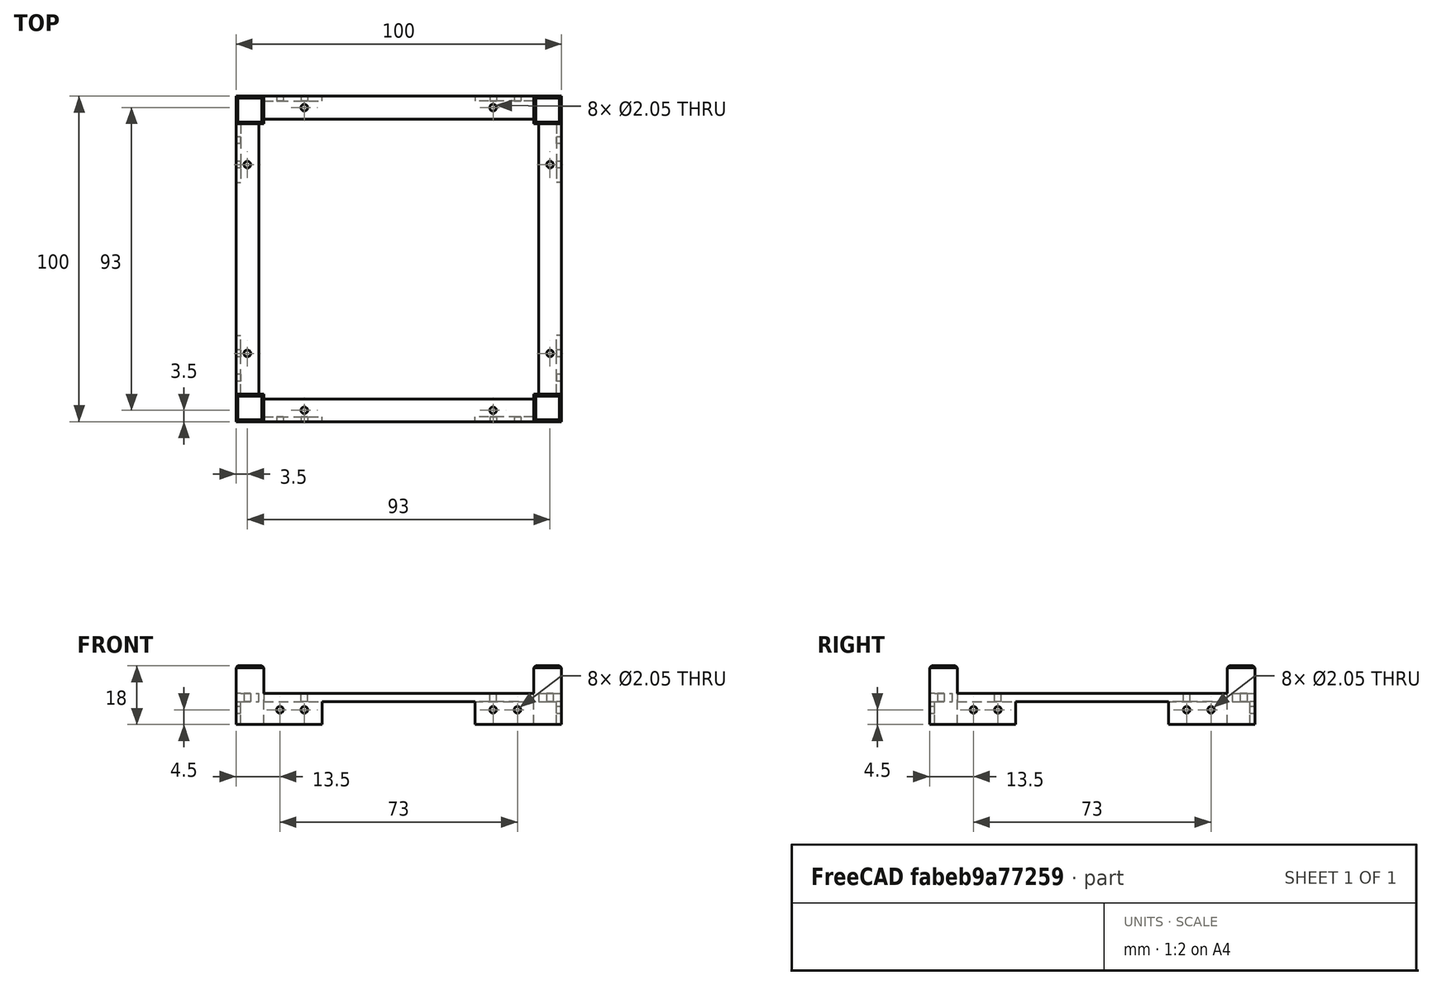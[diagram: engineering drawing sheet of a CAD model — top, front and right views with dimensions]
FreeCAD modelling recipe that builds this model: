
FCSTD DOCUMENT  (FreeCAD 0.20R29603 (Git))
Label: OpenSCAD_MyChassisModeling
License: All rights reserved
LicenseURL: http://en.wikipedia.org/wiki/All_rights_reserved
objects: Part::Box×72, Part::Fuse×56, Part::Cylinder×32, Part::Cut×17, Part::MultiFuse×13, Part::Mirroring×8, TechDraw::DrawViewDimension×5, TechDraw::DrawViewPart×3, TechDraw::DrawSVGTemplate×1, TechDraw::DrawViewAnnotation×1, TechDraw::DrawPage×1
note: 198 computed .brp shape members not serialized (recipe doc carries the construction recipe); baked Part::Feature solids carry a one-line shape summary decoded from their .brp

FEATURE [Part::Box] cube
  AttacherType = Attacher::AttachEngine3D
  Height = 2.5
  Length = 100
  Placement = pos=(-50,-3.5,-2.5) rot=(0,0,1;0rad)
  Width = 7
FEATURE [Part::Cylinder] cylinder
  Angle = 360
  AttacherType = Attacher::AttachEngine3D
  FirstAngle = 0
  Height = 100
  Placement = pos=(-29,0,-50) rot=(0,0,1;0rad)
  Radius = 1.025
  SecondAngle = 0
FEATURE [Part::Cylinder] cylinder001
  Angle = 360
  AttacherType = Attacher::AttachEngine3D
  FirstAngle = 0
  Height = 100
  Placement = pos=(29,0,-50) rot=(0,0,1;0rad)
  Radius = 1.025
  SecondAngle = 0
FEATURE [Part::Fuse] Group
  Base = -> cylinder
  Tool = -> cylinder001
FEATURE [Part::Cut] difference
  Base = -> cube
  Placement = pos=(0,46.5,0) rot=(0,0,1;0rad)
  Tool = -> Group
FEATURE [Part::Box] cube001
  AttacherType = Attacher::AttachEngine3D
  Height = 2.5
  Length = 100
  Placement = pos=(-50,-3.5,-2.5) rot=(0,0,1;0rad)
  Width = 7
FEATURE [Part::Cylinder] cylinder002
  Angle = 360
  AttacherType = Attacher::AttachEngine3D
  FirstAngle = 0
  Height = 100
  Placement = pos=(-29,0,-50) rot=(0,0,1;0rad)
  Radius = 1.025
  SecondAngle = 0
FEATURE [Part::Cylinder] cylinder003
  Angle = 360
  AttacherType = Attacher::AttachEngine3D
  FirstAngle = 0
  Height = 100
  Placement = pos=(29,0,-50) rot=(0,0,1;0rad)
  Radius = 1.025
  SecondAngle = 0
FEATURE [Part::Fuse] Group001
  Base = -> cylinder002
  Tool = -> cylinder003
FEATURE [Part::Cut] difference001
  Base = -> cube001
  Placement = pos=(0,46.5,0) rot=(0,0,1;0rad)
  Tool = -> Group001
FEATURE [Part::Fuse] Group002
  Base = -> difference
  Tool = -> difference001
FEATURE [Part::Box] cube002
  AttacherType = Attacher::AttachEngine3D
  Height = 2.5
  Length = 100
  Placement = pos=(-50,-3.5,-2.5) rot=(0,0,1;0rad)
  Width = 7
FEATURE [Part::Cylinder] cylinder004
  Angle = 360
  AttacherType = Attacher::AttachEngine3D
  FirstAngle = 0
  Height = 100
  Placement = pos=(-29,0,-50) rot=(0,0,1;0rad)
  Radius = 1.025
  SecondAngle = 0
FEATURE [Part::Cylinder] cylinder005
  Angle = 360
  AttacherType = Attacher::AttachEngine3D
  FirstAngle = 0
  Height = 100
  Placement = pos=(29,0,-50) rot=(0,0,1;0rad)
  Radius = 1.025
  SecondAngle = 0
FEATURE [Part::Fuse] Group003
  Base = -> cylinder004
  Tool = -> cylinder005
FEATURE [Part::Cut] difference002
  Base = -> cube002
  Placement = pos=(0,46.5,0) rot=(0,0,1;0rad)
  Tool = -> Group003
FEATURE [Part::Box] cube003
  AttacherType = Attacher::AttachEngine3D
  Height = 2.5
  Length = 100
  Placement = pos=(-50,-3.5,-2.5) rot=(0,0,1;0rad)
  Width = 7
FEATURE [Part::Cylinder] cylinder006
  Angle = 360
  AttacherType = Attacher::AttachEngine3D
  FirstAngle = 0
  Height = 100
  Placement = pos=(-29,0,-50) rot=(0,0,1;0rad)
  Radius = 1.025
  SecondAngle = 0
FEATURE [Part::Cylinder] cylinder007
  Angle = 360
  AttacherType = Attacher::AttachEngine3D
  FirstAngle = 0
  Height = 100
  Placement = pos=(29,0,-50) rot=(0,0,1;0rad)
  Radius = 1.025
  SecondAngle = 0
FEATURE [Part::Fuse] Group004
  Base = -> cylinder006
  Tool = -> cylinder007
FEATURE [Part::Cut] difference003
  Base = -> cube003
  Placement = pos=(-46.5,0,0) rot=(0,0,1;1.5708rad)
  Tool = -> Group004
FEATURE [Part::Fuse] Group005
  Base = -> difference002
  Tool = -> difference003
FEATURE [Part::Box] cube004
  AttacherType = Attacher::AttachEngine3D
  Height = 2.5
  Length = 100
  Placement = pos=(-50,-3.5,-2.5) rot=(0,0,1;0rad)
  Width = 7
FEATURE [Part::Cylinder] cylinder008
  Angle = 360
  AttacherType = Attacher::AttachEngine3D
  FirstAngle = 0
  Height = 100
  Placement = pos=(-29,0,-50) rot=(0,0,1;0rad)
  Radius = 1.025
  SecondAngle = 0
FEATURE [Part::Cylinder] cylinder009
  Angle = 360
  AttacherType = Attacher::AttachEngine3D
  FirstAngle = 0
  Height = 100
  Placement = pos=(29,0,-50) rot=(0,0,1;0rad)
  Radius = 1.025
  SecondAngle = 0
FEATURE [Part::Fuse] Group006
  Base = -> cylinder008
  Tool = -> cylinder009
FEATURE [Part::Cut] difference004
  Base = -> cube004
  Placement = pos=(0,46.5,0) rot=(0,0,1;0rad)
  Tool = -> Group006
FEATURE [Part::Box] cube005
  AttacherType = Attacher::AttachEngine3D
  Height = 2.5
  Length = 100
  Placement = pos=(-50,-3.5,-2.5) rot=(0,0,1;0rad)
  Width = 7
FEATURE [Part::Cylinder] cylinder010
  Angle = 360
  AttacherType = Attacher::AttachEngine3D
  FirstAngle = 0
  Height = 100
  Placement = pos=(-29,0,-50) rot=(0,0,1;0rad)
  Radius = 1.025
  SecondAngle = 0
FEATURE [Part::Cylinder] cylinder011
  Angle = 360
  AttacherType = Attacher::AttachEngine3D
  FirstAngle = 0
  Height = 100
  Placement = pos=(29,0,-50) rot=(0,0,1;0rad)
  Radius = 1.025
  SecondAngle = 0
FEATURE [Part::Fuse] Group007
  Base = -> cylinder010
  Tool = -> cylinder011
FEATURE [Part::Cut] difference005
  Base = -> cube005
  Placement = pos=(-5.7e-15,-46.5,0) rot=(0,0,1;3.14159rad)
  Tool = -> Group007
FEATURE [Part::Fuse] Group008
  Base = -> difference004
  Tool = -> difference005
FEATURE [Part::Box] cube006
  AttacherType = Attacher::AttachEngine3D
  Height = 2.5
  Length = 100
  Placement = pos=(-50,-3.5,-2.5) rot=(0,0,1;0rad)
  Width = 7
FEATURE [Part::Cylinder] cylinder012
  Angle = 360
  AttacherType = Attacher::AttachEngine3D
  FirstAngle = 0
  Height = 100
  Placement = pos=(-29,0,-50) rot=(0,0,1;0rad)
  Radius = 1.025
  SecondAngle = 0
FEATURE [Part::Cylinder] cylinder013
  Angle = 360
  AttacherType = Attacher::AttachEngine3D
  FirstAngle = 0
  Height = 100
  Placement = pos=(29,0,-50) rot=(0,0,1;0rad)
  Radius = 1.025
  SecondAngle = 0
FEATURE [Part::Fuse] Group009
  Base = -> cylinder012
  Tool = -> cylinder013
FEATURE [Part::Cut] difference006
  Base = -> cube006
  Placement = pos=(0,46.5,0) rot=(0,0,1;0rad)
  Tool = -> Group009
FEATURE [Part::Box] cube007
  AttacherType = Attacher::AttachEngine3D
  Height = 2.5
  Length = 100
  Placement = pos=(-50,-3.5,-2.5) rot=(0,0,1;0rad)
  Width = 7
FEATURE [Part::Cylinder] cylinder014
  Angle = 360
  AttacherType = Attacher::AttachEngine3D
  FirstAngle = 0
  Height = 100
  Placement = pos=(-29,0,-50) rot=(0,0,1;0rad)
  Radius = 1.025
  SecondAngle = 0
FEATURE [Part::Cylinder] cylinder015
  Angle = 360
  AttacherType = Attacher::AttachEngine3D
  FirstAngle = 0
  Height = 100
  Placement = pos=(29,0,-50) rot=(0,0,1;0rad)
  Radius = 1.025
  SecondAngle = 0
FEATURE [Part::Fuse] Group010
  Base = -> cylinder014
  Tool = -> cylinder015
FEATURE [Part::Cut] difference007
  Base = -> cube007
  Placement = pos=(46.5,0,0) rot=(0,0,-1;1.5708rad)
  Tool = -> Group010
FEATURE [Part::Fuse] Group011
  Base = -> difference006
  Tool = -> difference007
FEATURE [Part::MultiFuse] Group012
  Shapes = -> [Group002,Group005,Group008,Group011]
FEATURE [Part::Box] cube008
  AttacherType = Attacher::AttachEngine3D
  Height = 18
  Length = 8.5
  Placement = pos=(-4.25,-4.25,-18) rot=(0,0,1;0rad)
  Width = 8.5
FEATURE [Part::Box] cube009
  AttacherType = Attacher::AttachEngine3D
  Height = 100
  Length = 9.5
  Placement = pos=(-4.75,42.3466,-38.7141) rot=(1,0,0;0.785398rad)
  Width = 9.5
FEATURE [Part::Box] cube010
  AttacherType = Attacher::AttachEngine3D
  Height = 100
  Length = 9.5
  Placement = pos=(-42.3466,-4.75,-38.7141) rot=(0.357407,0.357407,0.862856;1.71777rad)
  Width = 9.5
FEATURE [Part::Fuse] Group013
  Base = -> cube009
  Tool = -> cube010
FEATURE [Part::Box] cube011
  AttacherType = Attacher::AttachEngine3D
  Height = 100
  Length = 9.5
  Placement = pos=(-4.75,42.3466,-38.7141) rot=(1,0,0;0.785398rad)
  Width = 9.5
FEATURE [Part::Box] cube012
  AttacherType = Attacher::AttachEngine3D
  Height = 100
  Length = 9.5
  Placement = pos=(4.75,-42.3466,-38.7141) rot=(0,0.382683,0.92388;3.14159rad)
  Width = 9.5
FEATURE [Part::Fuse] Group014
  Base = -> cube011
  Tool = -> cube012
FEATURE [Part::Box] cube013
  AttacherType = Attacher::AttachEngine3D
  Height = 100
  Length = 9.5
  Placement = pos=(-4.75,42.3466,-38.7141) rot=(1,0,0;0.785398rad)
  Width = 9.5
FEATURE [Part::Box] cube014
  AttacherType = Attacher::AttachEngine3D
  Height = 100
  Length = 9.5
  Placement = pos=(42.3466,4.75,-38.7141) rot=(0.357407,-0.357407,-0.862856;1.71777rad)
  Width = 9.5
FEATURE [Part::Fuse] Group015
  Base = -> cube013
  Tool = -> cube014
FEATURE [Part::MultiFuse] Group016
  Shapes = -> [Group013,Group014,Group015]
FEATURE [Part::Cut] difference008
  Base = -> cube008
  Placement = pos=(-45.75,-45.75,8.5) rot=(0,0,1;0rad)
  Tool = -> Group016
FEATURE [Part::Box] cube015
  AttacherType = Attacher::AttachEngine3D
  Height = 18
  Length = 8.5
  Placement = pos=(-4.25,-4.25,-18) rot=(0,0,1;0rad)
  Width = 8.5
FEATURE [Part::Box] cube016
  AttacherType = Attacher::AttachEngine3D
  Height = 100
  Length = 9.5
  Placement = pos=(-4.75,42.3466,-38.7141) rot=(1,0,0;0.785398rad)
  Width = 9.5
FEATURE [Part::Box] cube017
  AttacherType = Attacher::AttachEngine3D
  Height = 100
  Length = 9.5
  Placement = pos=(-42.3466,-4.75,-38.7141) rot=(0.357407,0.357407,0.862856;1.71777rad)
  Width = 9.5
FEATURE [Part::Fuse] Group017
  Base = -> cube016
  Tool = -> cube017
FEATURE [Part::Box] cube018
  AttacherType = Attacher::AttachEngine3D
  Height = 100
  Length = 9.5
  Placement = pos=(-4.75,42.3466,-38.7141) rot=(1,0,0;0.785398rad)
  Width = 9.5
FEATURE [Part::Box] cube019
  AttacherType = Attacher::AttachEngine3D
  Height = 100
  Length = 9.5
  Placement = pos=(4.75,-42.3466,-38.7141) rot=(0,0.382683,0.92388;3.14159rad)
  Width = 9.5
FEATURE [Part::Fuse] Group018
  Base = -> cube018
  Tool = -> cube019
FEATURE [Part::Box] cube020
  AttacherType = Attacher::AttachEngine3D
  Height = 100
  Length = 9.5
  Placement = pos=(-4.75,42.3466,-38.7141) rot=(1,0,0;0.785398rad)
  Width = 9.5
FEATURE [Part::Box] cube021
  AttacherType = Attacher::AttachEngine3D
  Height = 100
  Length = 9.5
  Placement = pos=(42.3466,4.75,-38.7141) rot=(0.357407,-0.357407,-0.862856;1.71777rad)
  Width = 9.5
FEATURE [Part::Fuse] Group019
  Base = -> cube020
  Tool = -> cube021
FEATURE [Part::MultiFuse] Group020
  Shapes = -> [Group017,Group018,Group019]
FEATURE [Part::Cut] difference009
  Base = -> cube015
  Placement = pos=(-45.75,-45.75,8.5) rot=(0,0,1;0rad)
  Tool = -> Group020
FEATURE [Part::Fuse] Group021
  Base = -> difference008
  Tool = -> difference009
FEATURE [Part::Box] cube022
  AttacherType = Attacher::AttachEngine3D
  Height = 18
  Length = 8.5
  Placement = pos=(-4.25,-4.25,-18) rot=(0,0,1;0rad)
  Width = 8.5
FEATURE [Part::Box] cube023
  AttacherType = Attacher::AttachEngine3D
  Height = 100
  Length = 9.5
  Placement = pos=(-4.75,42.3466,-38.7141) rot=(1,0,0;0.785398rad)
  Width = 9.5
FEATURE [Part::Box] cube024
  AttacherType = Attacher::AttachEngine3D
  Height = 100
  Length = 9.5
  Placement = pos=(-42.3466,-4.75,-38.7141) rot=(0.357407,0.357407,0.862856;1.71777rad)
  Width = 9.5
FEATURE [Part::Fuse] Group022
  Base = -> cube023
  Tool = -> cube024
FEATURE [Part::Box] cube025
  AttacherType = Attacher::AttachEngine3D
  Height = 100
  Length = 9.5
  Placement = pos=(-4.75,42.3466,-38.7141) rot=(1,0,0;0.785398rad)
  Width = 9.5
FEATURE [Part::Box] cube026
  AttacherType = Attacher::AttachEngine3D
  Height = 100
  Length = 9.5
  Placement = pos=(4.75,-42.3466,-38.7141) rot=(0,0.382683,0.92388;3.14159rad)
  Width = 9.5
FEATURE [Part::Fuse] Group023
  Base = -> cube025
  Tool = -> cube026
FEATURE [Part::Box] cube027
  AttacherType = Attacher::AttachEngine3D
  Height = 100
  Length = 9.5
  Placement = pos=(-4.75,42.3466,-38.7141) rot=(1,0,0;0.785398rad)
  Width = 9.5
FEATURE [Part::Box] cube028
  AttacherType = Attacher::AttachEngine3D
  Height = 100
  Length = 9.5
  Placement = pos=(42.3466,4.75,-38.7141) rot=(0.357407,-0.357407,-0.862856;1.71777rad)
  Width = 9.5
FEATURE [Part::Fuse] Group024
  Base = -> cube027
  Tool = -> cube028
FEATURE [Part::MultiFuse] Group025
  Shapes = -> [Group022,Group023,Group024]
FEATURE [Part::Cut] difference010
  Base = -> cube022
  Placement = pos=(-45.75,-45.75,8.5) rot=(0,0,1;0rad)
  Tool = -> Group025
FEATURE [Part::Box] cube029
  AttacherType = Attacher::AttachEngine3D
  Height = 18
  Length = 8.5
  Placement = pos=(-4.25,-4.25,-18) rot=(0,0,1;0rad)
  Width = 8.5
FEATURE [Part::Box] cube030
  AttacherType = Attacher::AttachEngine3D
  Height = 100
  Length = 9.5
  Placement = pos=(-4.75,42.3466,-38.7141) rot=(1,0,0;0.785398rad)
  Width = 9.5
FEATURE [Part::Box] cube031
  AttacherType = Attacher::AttachEngine3D
  Height = 100
  Length = 9.5
  Placement = pos=(-42.3466,-4.75,-38.7141) rot=(0.357407,0.357407,0.862856;1.71777rad)
  Width = 9.5
FEATURE [Part::Fuse] Group026
  Base = -> cube030
  Tool = -> cube031
FEATURE [Part::Box] cube032
  AttacherType = Attacher::AttachEngine3D
  Height = 100
  Length = 9.5
  Placement = pos=(-4.75,42.3466,-38.7141) rot=(1,0,0;0.785398rad)
  Width = 9.5
FEATURE [Part::Box] cube033
  AttacherType = Attacher::AttachEngine3D
  Height = 100
  Length = 9.5
  Placement = pos=(4.75,-42.3466,-38.7141) rot=(0,0.382683,0.92388;3.14159rad)
  Width = 9.5
FEATURE [Part::Fuse] Group027
  Base = -> cube032
  Tool = -> cube033
FEATURE [Part::Box] cube034
  AttacherType = Attacher::AttachEngine3D
  Height = 100
  Length = 9.5
  Placement = pos=(-4.75,42.3466,-38.7141) rot=(1,0,0;0.785398rad)
  Width = 9.5
FEATURE [Part::Box] cube035
  AttacherType = Attacher::AttachEngine3D
  Height = 100
  Length = 9.5
  Placement = pos=(42.3466,4.75,-38.7141) rot=(0.357407,-0.357407,-0.862856;1.71777rad)
  Width = 9.5
FEATURE [Part::Fuse] Group028
  Base = -> cube034
  Tool = -> cube035
FEATURE [Part::MultiFuse] Group029
  Shapes = -> [Group026,Group027,Group028]
FEATURE [Part::Cut] difference011
  Base = -> cube029
  Placement = pos=(45.75,-45.75,8.5) rot=(0,0,1;1.5708rad)
  Tool = -> Group029
FEATURE [Part::Fuse] Group030
  Base = -> difference010
  Tool = -> difference011
FEATURE [Part::Box] cube036
  AttacherType = Attacher::AttachEngine3D
  Height = 18
  Length = 8.5
  Placement = pos=(-4.25,-4.25,-18) rot=(0,0,1;0rad)
  Width = 8.5
FEATURE [Part::Box] cube037
  AttacherType = Attacher::AttachEngine3D
  Height = 100
  Length = 9.5
  Placement = pos=(-4.75,42.3466,-38.7141) rot=(1,0,0;0.785398rad)
  Width = 9.5
FEATURE [Part::Box] cube038
  AttacherType = Attacher::AttachEngine3D
  Height = 100
  Length = 9.5
  Placement = pos=(-42.3466,-4.75,-38.7141) rot=(0.357407,0.357407,0.862856;1.71777rad)
  Width = 9.5
FEATURE [Part::Fuse] Group031
  Base = -> cube037
  Tool = -> cube038
FEATURE [Part::Box] cube039
  AttacherType = Attacher::AttachEngine3D
  Height = 100
  Length = 9.5
  Placement = pos=(-4.75,42.3466,-38.7141) rot=(1,0,0;0.785398rad)
  Width = 9.5
FEATURE [Part::Box] cube040
  AttacherType = Attacher::AttachEngine3D
  Height = 100
  Length = 9.5
  Placement = pos=(4.75,-42.3466,-38.7141) rot=(0,0.382683,0.92388;3.14159rad)
  Width = 9.5
FEATURE [Part::Fuse] Group032
  Base = -> cube039
  Tool = -> cube040
FEATURE [Part::Box] cube041
  AttacherType = Attacher::AttachEngine3D
  Height = 100
  Length = 9.5
  Placement = pos=(-4.75,42.3466,-38.7141) rot=(1,0,0;0.785398rad)
  Width = 9.5
FEATURE [Part::Box] cube042
  AttacherType = Attacher::AttachEngine3D
  Height = 100
  Length = 9.5
  Placement = pos=(42.3466,4.75,-38.7141) rot=(0.357407,-0.357407,-0.862856;1.71777rad)
  Width = 9.5
FEATURE [Part::Fuse] Group033
  Base = -> cube041
  Tool = -> cube042
FEATURE [Part::MultiFuse] Group034
  Shapes = -> [Group031,Group032,Group033]
FEATURE [Part::Cut] difference012
  Base = -> cube036
  Placement = pos=(-45.75,-45.75,8.5) rot=(0,0,1;0rad)
  Tool = -> Group034
FEATURE [Part::Box] cube043
  AttacherType = Attacher::AttachEngine3D
  Height = 18
  Length = 8.5
  Placement = pos=(-4.25,-4.25,-18) rot=(0,0,1;0rad)
  Width = 8.5
FEATURE [Part::Box] cube044
  AttacherType = Attacher::AttachEngine3D
  Height = 100
  Length = 9.5
  Placement = pos=(-4.75,42.3466,-38.7141) rot=(1,0,0;0.785398rad)
  Width = 9.5
FEATURE [Part::Box] cube045
  AttacherType = Attacher::AttachEngine3D
  Height = 100
  Length = 9.5
  Placement = pos=(-42.3466,-4.75,-38.7141) rot=(0.357407,0.357407,0.862856;1.71777rad)
  Width = 9.5
FEATURE [Part::Fuse] Group035
  Base = -> cube044
  Tool = -> cube045
FEATURE [Part::Box] cube046
  AttacherType = Attacher::AttachEngine3D
  Height = 100
  Length = 9.5
  Placement = pos=(-4.75,42.3466,-38.7141) rot=(1,0,0;0.785398rad)
  Width = 9.5
FEATURE [Part::Box] cube047
  AttacherType = Attacher::AttachEngine3D
  Height = 100
  Length = 9.5
  Placement = pos=(4.75,-42.3466,-38.7141) rot=(0,0.382683,0.92388;3.14159rad)
  Width = 9.5
FEATURE [Part::Fuse] Group036
  Base = -> cube046
  Tool = -> cube047
FEATURE [Part::Box] cube048
  AttacherType = Attacher::AttachEngine3D
  Height = 100
  Length = 9.5
  Placement = pos=(-4.75,42.3466,-38.7141) rot=(1,0,0;0.785398rad)
  Width = 9.5
FEATURE [Part::Box] cube049
  AttacherType = Attacher::AttachEngine3D
  Height = 100
  Length = 9.5
  Placement = pos=(42.3466,4.75,-38.7141) rot=(0.357407,-0.357407,-0.862856;1.71777rad)
  Width = 9.5
FEATURE [Part::Fuse] Group037
  Base = -> cube048
  Tool = -> cube049
FEATURE [Part::MultiFuse] Group038
  Shapes = -> [Group035,Group036,Group037]
FEATURE [Part::Cut] difference013
  Base = -> cube043
  Placement = pos=(45.75,45.75,8.5) rot=(0,0,1;3.14159rad)
  Tool = -> Group038
FEATURE [Part::Fuse] Group039
  Base = -> difference012
  Tool = -> difference013
FEATURE [Part::Box] cube050
  AttacherType = Attacher::AttachEngine3D
  Height = 18
  Length = 8.5
  Placement = pos=(-4.25,-4.25,-18) rot=(0,0,1;0rad)
  Width = 8.5
FEATURE [Part::Box] cube051
  AttacherType = Attacher::AttachEngine3D
  Height = 100
  Length = 9.5
  Placement = pos=(-4.75,42.3466,-38.7141) rot=(1,0,0;0.785398rad)
  Width = 9.5
FEATURE [Part::Box] cube052
  AttacherType = Attacher::AttachEngine3D
  Height = 100
  Length = 9.5
  Placement = pos=(-42.3466,-4.75,-38.7141) rot=(0.357407,0.357407,0.862856;1.71777rad)
  Width = 9.5
FEATURE [Part::Fuse] Group040
  Base = -> cube051
  Tool = -> cube052
FEATURE [Part::Box] cube053
  AttacherType = Attacher::AttachEngine3D
  Height = 100
  Length = 9.5
  Placement = pos=(-4.75,42.3466,-38.7141) rot=(1,0,0;0.785398rad)
  Width = 9.5
FEATURE [Part::Box] cube054
  AttacherType = Attacher::AttachEngine3D
  Height = 100
  Length = 9.5
  Placement = pos=(4.75,-42.3466,-38.7141) rot=(0,0.382683,0.92388;3.14159rad)
  Width = 9.5
FEATURE [Part::Fuse] Group041
  Base = -> cube053
  Tool = -> cube054
FEATURE [Part::Box] cube055
  AttacherType = Attacher::AttachEngine3D
  Height = 100
  Length = 9.5
  Placement = pos=(-4.75,42.3466,-38.7141) rot=(1,0,0;0.785398rad)
  Width = 9.5
FEATURE [Part::Box] cube056
  AttacherType = Attacher::AttachEngine3D
  Height = 100
  Length = 9.5
  Placement = pos=(42.3466,4.75,-38.7141) rot=(0.357407,-0.357407,-0.862856;1.71777rad)
  Width = 9.5
FEATURE [Part::Fuse] Group042
  Base = -> cube055
  Tool = -> cube056
FEATURE [Part::MultiFuse] Group043
  Shapes = -> [Group040,Group041,Group042]
FEATURE [Part::Cut] difference014
  Base = -> cube050
  Placement = pos=(-45.75,-45.75,8.5) rot=(0,0,1;0rad)
  Tool = -> Group043
FEATURE [Part::Box] cube057
  AttacherType = Attacher::AttachEngine3D
  Height = 18
  Length = 8.5
  Placement = pos=(-4.25,-4.25,-18) rot=(0,0,1;0rad)
  Width = 8.5
FEATURE [Part::Box] cube058
  AttacherType = Attacher::AttachEngine3D
  Height = 100
  Length = 9.5
  Placement = pos=(-4.75,42.3466,-38.7141) rot=(1,0,0;0.785398rad)
  Width = 9.5
FEATURE [Part::Box] cube059
  AttacherType = Attacher::AttachEngine3D
  Height = 100
  Length = 9.5
  Placement = pos=(-42.3466,-4.75,-38.7141) rot=(0.357407,0.357407,0.862856;1.71777rad)
  Width = 9.5
FEATURE [Part::Fuse] Group044
  Base = -> cube058
  Tool = -> cube059
FEATURE [Part::Box] cube060
  AttacherType = Attacher::AttachEngine3D
  Height = 100
  Length = 9.5
  Placement = pos=(-4.75,42.3466,-38.7141) rot=(1,0,0;0.785398rad)
  Width = 9.5
FEATURE [Part::Box] cube061
  AttacherType = Attacher::AttachEngine3D
  Height = 100
  Length = 9.5
  Placement = pos=(4.75,-42.3466,-38.7141) rot=(0,0.382683,0.92388;3.14159rad)
  Width = 9.5
FEATURE [Part::Fuse] Group045
  Base = -> cube060
  Tool = -> cube061
FEATURE [Part::Box] cube062
  AttacherType = Attacher::AttachEngine3D
  Height = 100
  Length = 9.5
  Placement = pos=(-4.75,42.3466,-38.7141) rot=(1,0,0;0.785398rad)
  Width = 9.5
FEATURE [Part::Box] cube063
  AttacherType = Attacher::AttachEngine3D
  Height = 100
  Length = 9.5
  Placement = pos=(42.3466,4.75,-38.7141) rot=(0.357407,-0.357407,-0.862856;1.71777rad)
  Width = 9.5
FEATURE [Part::Fuse] Group046
  Base = -> cube062
  Tool = -> cube063
FEATURE [Part::MultiFuse] Group047
  Shapes = -> [Group044,Group045,Group046]
FEATURE [Part::Cut] difference015
  Base = -> cube057
  Placement = pos=(-45.75,45.75,8.5) rot=(0,0,-1;1.5708rad)
  Tool = -> Group047
FEATURE [Part::Fuse] Group048
  Base = -> difference014
  Tool = -> difference015
FEATURE [Part::MultiFuse] Group049
  Shapes = -> [Group021,Group030,Group039,Group048]
FEATURE [Part::Box] cube064
  AttacherType = Attacher::AttachEngine3D
  Height = 9.5
  Length = 1.5
  Placement = pos=(48.5,-41.5,-9.5) rot=(0,0,1;0rad)
  Width = 18
FEATURE [Part::Box] cube065
  AttacherType = Attacher::AttachEngine3D
  Height = 9.5
  Length = 1.5
  Placement = pos=(48.5,-41.5,-9.5) rot=(0,0,1;0rad)
  Width = 18
FEATURE [Part::Mirroring] mirr_cube065  label="mirrored cube065"
  Base = (0,0,0)
  Normal = (0,1,0)
  Source = -> cube065
FEATURE [Part::Fuse] Group050
  Base = -> cube064
  Tool = -> mirr_cube065
FEATURE [Part::Box] cube066
  AttacherType = Attacher::AttachEngine3D
  Height = 9.5
  Length = 1.5
  Placement = pos=(48.5,-41.5,-9.5) rot=(0,0,1;0rad)
  Width = 18
FEATURE [Part::Box] cube067
  AttacherType = Attacher::AttachEngine3D
  Height = 9.5
  Length = 1.5
  Placement = pos=(48.5,-41.5,-9.5) rot=(0,0,1;0rad)
  Width = 18
FEATURE [Part::Mirroring] mirr_cube067  label="mirrored cube067"
  Base = (0,0,0)
  Normal = (0,1,0)
  Source = -> cube067
FEATURE [Part::Fuse] Group051
  Base = -> cube066
  Placement = pos=(0,0,0) rot=(0,0,1;1.5708rad)
  Tool = -> mirr_cube067
FEATURE [Part::Box] cube068
  AttacherType = Attacher::AttachEngine3D
  Height = 9.5
  Length = 1.5
  Placement = pos=(48.5,-41.5,-9.5) rot=(0,0,1;0rad)
  Width = 18
FEATURE [Part::Box] cube069
  AttacherType = Attacher::AttachEngine3D
  Height = 9.5
  Length = 1.5
  Placement = pos=(48.5,-41.5,-9.5) rot=(0,0,1;0rad)
  Width = 18
FEATURE [Part::Mirroring] mirr_cube069  label="mirrored cube069"
  Base = (0,0,0)
  Normal = (0,1,0)
  Source = -> cube069
FEATURE [Part::Fuse] Group052
  Base = -> cube068
  Placement = pos=(0,0,0) rot=(0,0,1;3.14159rad)
  Tool = -> mirr_cube069
FEATURE [Part::Box] cube070
  AttacherType = Attacher::AttachEngine3D
  Height = 9.5
  Length = 1.5
  Placement = pos=(48.5,-41.5,-9.5) rot=(0,0,1;0rad)
  Width = 18
FEATURE [Part::Box] cube071
  AttacherType = Attacher::AttachEngine3D
  Height = 9.5
  Length = 1.5
  Placement = pos=(48.5,-41.5,-9.5) rot=(0,0,1;0rad)
  Width = 18
FEATURE [Part::Mirroring] mirr_cube071  label="mirrored cube071"
  Base = (0,0,0)
  Normal = (0,1,0)
  Source = -> cube071
FEATURE [Part::Fuse] Group053
  Base = -> cube070
  Placement = pos=(0,0,0) rot=(0,0,-1;1.5708rad)
  Tool = -> mirr_cube071
FEATURE [Part::MultiFuse] Group054
  Shapes = -> [Group050,Group051,Group052,Group053]
FEATURE [Part::Cylinder] cylinder016
  Angle = 360
  AttacherType = Attacher::AttachEngine3D
  FirstAngle = 0
  Height = 500
  Placement = pos=(-250,-36.5,-5) rot=(0,1,0;1.5708rad)
  Radius = 1.025
  SecondAngle = 0
FEATURE [Part::Cylinder] cylinder017
  Angle = 360
  AttacherType = Attacher::AttachEngine3D
  FirstAngle = 0
  Height = 500
  Placement = pos=(-250,-29,-5) rot=(0,1,0;1.5708rad)
  Radius = 1.025
  SecondAngle = 0
FEATURE [Part::Fuse] Group055
  Base = -> cylinder016
  Tool = -> cylinder017
FEATURE [Part::Cylinder] cylinder018
  Angle = 360
  AttacherType = Attacher::AttachEngine3D
  FirstAngle = 0
  Height = 500
  Placement = pos=(-250,-36.5,-5) rot=(0,1,0;1.5708rad)
  Radius = 1.025
  SecondAngle = 0
FEATURE [Part::Cylinder] cylinder019
  Angle = 360
  AttacherType = Attacher::AttachEngine3D
  FirstAngle = 0
  Height = 500
  Placement = pos=(-250,-29,-5) rot=(0,1,0;1.5708rad)
  Radius = 1.025
  SecondAngle = 0
FEATURE [Part::Fuse] Group056
  Base = -> cylinder018
  Tool = -> cylinder019
FEATURE [Part::Mirroring] mirr_Group056  label="mirrored Group056"
  Base = (0,0,0)
  Normal = (0,1,0)
  Source = -> Group056
FEATURE [Part::Fuse] Group057
  Base = -> Group055
  Tool = -> mirr_Group056
FEATURE [Part::Cylinder] cylinder020
  Angle = 360
  AttacherType = Attacher::AttachEngine3D
  FirstAngle = 0
  Height = 500
  Placement = pos=(-250,-36.5,-5) rot=(0,1,0;1.5708rad)
  Radius = 1.025
  SecondAngle = 0
FEATURE [Part::Cylinder] cylinder021
  Angle = 360
  AttacherType = Attacher::AttachEngine3D
  FirstAngle = 0
  Height = 500
  Placement = pos=(-250,-29,-5) rot=(0,1,0;1.5708rad)
  Radius = 1.025
  SecondAngle = 0
FEATURE [Part::Fuse] Group058
  Base = -> cylinder020
  Tool = -> cylinder021
FEATURE [Part::Cylinder] cylinder022
  Angle = 360
  AttacherType = Attacher::AttachEngine3D
  FirstAngle = 0
  Height = 500
  Placement = pos=(-250,-36.5,-5) rot=(0,1,0;1.5708rad)
  Radius = 1.025
  SecondAngle = 0
FEATURE [Part::Cylinder] cylinder023
  Angle = 360
  AttacherType = Attacher::AttachEngine3D
  FirstAngle = 0
  Height = 500
  Placement = pos=(-250,-29,-5) rot=(0,1,0;1.5708rad)
  Radius = 1.025
  SecondAngle = 0
FEATURE [Part::Fuse] Group059
  Base = -> cylinder022
  Tool = -> cylinder023
FEATURE [Part::Mirroring] mirr_Group059  label="mirrored Group059"
  Base = (0,0,0)
  Normal = (0,1,0)
  Source = -> Group059
FEATURE [Part::Fuse] Group060
  Base = -> Group058
  Placement = pos=(0,0,0) rot=(0,0,1;1.5708rad)
  Tool = -> mirr_Group059
FEATURE [Part::Cylinder] cylinder024
  Angle = 360
  AttacherType = Attacher::AttachEngine3D
  FirstAngle = 0
  Height = 500
  Placement = pos=(-250,-36.5,-5) rot=(0,1,0;1.5708rad)
  Radius = 1.025
  SecondAngle = 0
FEATURE [Part::Cylinder] cylinder025
  Angle = 360
  AttacherType = Attacher::AttachEngine3D
  FirstAngle = 0
  Height = 500
  Placement = pos=(-250,-29,-5) rot=(0,1,0;1.5708rad)
  Radius = 1.025
  SecondAngle = 0
FEATURE [Part::Fuse] Group061
  Base = -> cylinder024
  Tool = -> cylinder025
FEATURE [Part::Cylinder] cylinder026
  Angle = 360
  AttacherType = Attacher::AttachEngine3D
  FirstAngle = 0
  Height = 500
  Placement = pos=(-250,-36.5,-5) rot=(0,1,0;1.5708rad)
  Radius = 1.025
  SecondAngle = 0
FEATURE [Part::Cylinder] cylinder027
  Angle = 360
  AttacherType = Attacher::AttachEngine3D
  FirstAngle = 0
  Height = 500
  Placement = pos=(-250,-29,-5) rot=(0,1,0;1.5708rad)
  Radius = 1.025
  SecondAngle = 0
FEATURE [Part::Fuse] Group062
  Base = -> cylinder026
  Tool = -> cylinder027
FEATURE [Part::Mirroring] mirr_Group062  label="mirrored Group062"
  Base = (0,0,0)
  Normal = (0,1,0)
  Source = -> Group062
FEATURE [Part::Fuse] Group063
  Base = -> Group061
  Placement = pos=(0,0,0) rot=(0,0,1;3.14159rad)
  Tool = -> mirr_Group062
FEATURE [Part::Cylinder] cylinder028
  Angle = 360
  AttacherType = Attacher::AttachEngine3D
  FirstAngle = 0
  Height = 500
  Placement = pos=(-250,-36.5,-5) rot=(0,1,0;1.5708rad)
  Radius = 1.025
  SecondAngle = 0
FEATURE [Part::Cylinder] cylinder029
  Angle = 360
  AttacherType = Attacher::AttachEngine3D
  FirstAngle = 0
  Height = 500
  Placement = pos=(-250,-29,-5) rot=(0,1,0;1.5708rad)
  Radius = 1.025
  SecondAngle = 0
FEATURE [Part::Fuse] Group064
  Base = -> cylinder028
  Tool = -> cylinder029
FEATURE [Part::Cylinder] cylinder030
  Angle = 360
  AttacherType = Attacher::AttachEngine3D
  FirstAngle = 0
  Height = 500
  Placement = pos=(-250,-36.5,-5) rot=(0,1,0;1.5708rad)
  Radius = 1.025
  SecondAngle = 0
FEATURE [Part::Cylinder] cylinder031
  Angle = 360
  AttacherType = Attacher::AttachEngine3D
  FirstAngle = 0
  Height = 500
  Placement = pos=(-250,-29,-5) rot=(0,1,0;1.5708rad)
  Radius = 1.025
  SecondAngle = 0
FEATURE [Part::Fuse] Group065
  Base = -> cylinder030
  Tool = -> cylinder031
FEATURE [Part::Mirroring] mirr_Group065  label="mirrored Group065"
  Base = (0,0,0)
  Normal = (0,1,0)
  Source = -> Group065
FEATURE [Part::Fuse] Group066
  Base = -> Group064
  Placement = pos=(0,0,0) rot=(0,0,-1;1.5708rad)
  Tool = -> mirr_Group065
FEATURE [Part::MultiFuse] Group067
  Shapes = -> [Group057,Group060,Group063,Group066]
FEATURE [Part::Cut] difference016
  Base = -> Group054
  Tool = -> Group067
FEATURE [Part::MultiFuse] union
  Shapes = -> [Group012,Group049,difference016]
FEATURE [TechDraw::DrawSVGTemplate] Template
  Height = 297
  Orientation = 1
  Width = 420
FEATURE [TechDraw::DrawViewPart] View  label="Top View"
  CoarseView = false
  Direction = (0,0,1)
  Focus = 100
  HardHidden = false
  IsoCount = 0
  IsoHidden = false
  IsoVisible = false
  LockPosition = false
  Perspective = false
  Rotation = 0
  ScaleType = 0
  SeamHidden = false
  SeamVisible = true
  SmoothHidden = false
  SmoothVisible = true
  Source = -> [union]
  X = 153.114
  XDirection = (1,0,0)
  Y = 183.176
FEATURE [TechDraw::DrawViewPart] View002
  CoarseView = false
  Direction = (0.577,0.577,0.577)
  Focus = 100
  HardHidden = false
  IsoCount = 0
  IsoHidden = false
  IsoVisible = false
  LockPosition = false
  Perspective = false
  Rotation = 0
  ScaleType = 0
  SeamHidden = false
  SeamVisible = true
  SmoothHidden = false
  SmoothVisible = true
  Source = -> [union]
  X = 301.223
  XDirection = (-0.707,0.707,0)
  Y = 185.009
FEATURE [TechDraw::DrawViewDimension] Dimension
  AngleOverride = false
  Arbitrary = false
  ArbitraryTolerances = false
  EqualTolerance = true
  ExtensionAngle = 0
  FormatSpec = %.2w
  FormatSpecOverTolerance = %+.2w
  FormatSpecUnderTolerance = %+.2w
  Inverted = false
  LineAngle = 0
  LockPosition = false
  MeasureType = 1
  OverTolerance = 0
  References2D = -> [View]
  Rotation = 0
  ScaleType = 0
  TheoreticalExact = false
  Type = 1
  UnderTolerance = 0
  X = 0.261474
  Y = 71.1954
FEATURE [TechDraw::DrawViewDimension] Dimension001
  AngleOverride = false
  Arbitrary = false
  ArbitraryTolerances = false
  EqualTolerance = true
  ExtensionAngle = 0
  FormatSpec = %.2w
  FormatSpecOverTolerance = %+.2w
  FormatSpecUnderTolerance = %+.2w
  Inverted = false
  LineAngle = 0
  LockPosition = false
  MeasureType = 1
  OverTolerance = 0
  References2D = -> [View]
  Rotation = 0
  ScaleType = 0
  TheoreticalExact = false
  Type = 2
  UnderTolerance = 0
  X = -63.4049
  Y = 0.025241
FEATURE [TechDraw::DrawViewPart] View003  label="Side View"
  CoarseView = false
  Direction = (0,1,0)
  Focus = 100
  HardHidden = false
  IsoCount = 0
  IsoHidden = false
  IsoVisible = false
  LockPosition = false
  Perspective = false
  Rotation = 0
  ScaleType = 0
  SeamHidden = false
  SeamVisible = true
  SmoothHidden = false
  SmoothVisible = true
  Source = -> [union]
  X = 286.63
  XDirection = (-1,0,-0.001)
  Y = 70.574
FEATURE [TechDraw::DrawViewDimension] Dimension003
  AngleOverride = false
  Arbitrary = false
  ArbitraryTolerances = false
  EqualTolerance = true
  ExtensionAngle = 0
  FormatSpec = %.2w
  FormatSpecOverTolerance = %+.2w
  FormatSpecUnderTolerance = %+.2w
  Inverted = false
  LineAngle = 0
  LockPosition = false
  MeasureType = 1
  OverTolerance = 0
  References2D = -> [View003]
  Rotation = 0
  ScaleType = 0
  TheoreticalExact = false
  Type = 2
  UnderTolerance = 0
  X = 62.7021
  Y = 1.79342
FEATURE [TechDraw::DrawViewAnnotation] Annotation
  Font = osifont
  LineSpace = 80
  LockPosition = false
  MaxWidth = -1
  Rotation = 0
  ScaleType = 0
  Text = Unit: Millimeters (mm) | - All holes are threaded for M2.5x0.45 screw | - Tolerance follow ISO 2768 standards | - NO retaining sharp corners required
  TextSize = 5
  TextStyle = 0
  X = 149.96
  Y = 71.5251
FEATURE [TechDraw::DrawViewDimension] Dimension005
  AngleOverride = false
  Arbitrary = false
  ArbitraryTolerances = false
  EqualTolerance = true
  ExtensionAngle = 0
  FormatSpec = ⌀%.2w
  FormatSpecOverTolerance = %+.2w
  FormatSpecUnderTolerance = %+.2w
  Inverted = false
  LineAngle = 0
  LockPosition = false
  MeasureType = 1
  OverTolerance = 0
  References2D = -> [View]
  Rotation = 0
  ScaleType = 0
  TheoreticalExact = false
  Type = 5
  UnderTolerance = 0
  X = 62.3615
  Y = 34.776
FEATURE [TechDraw::DrawViewDimension] Dimension006
  AngleOverride = false
  Arbitrary = false
  ArbitraryTolerances = false
  EqualTolerance = true
  ExtensionAngle = 0
  FormatSpec = ⌀%.2w
  FormatSpecOverTolerance = %+.2w
  FormatSpecUnderTolerance = %+.2w
  Inverted = false
  LineAngle = 0
  LockPosition = false
  MeasureType = 1
  OverTolerance = 0
  References2D = -> [View003]
  Rotation = 0
  ScaleType = 0
  TheoreticalExact = false
  Type = 5
  UnderTolerance = 0
  X = -16.9777
  Y = 18.7027
FEATURE [TechDraw::DrawPage] Page  label="TechnicalDrawing"
  KeepUpdated = true
  NextBalloonIndex = 1
  ProjectionType = 0
  Template = -> Template
  Views = -> [View,View002,Dimension,Dimension001,View003,Dimension003,Annotation,Dimension005,Dimension006]
